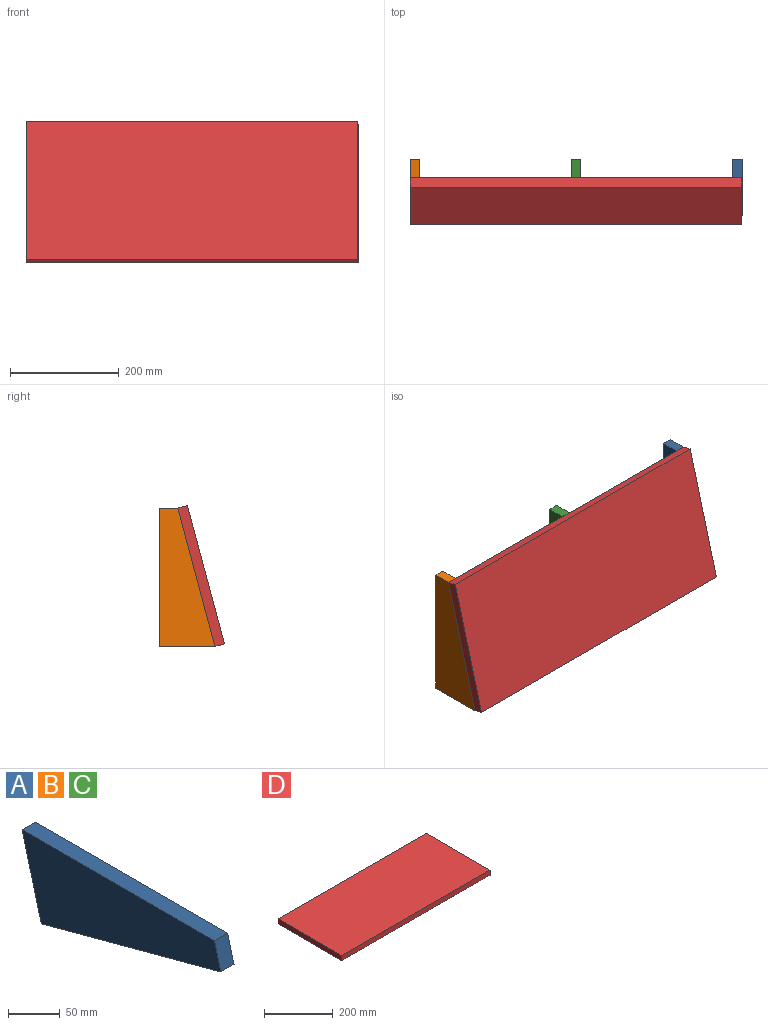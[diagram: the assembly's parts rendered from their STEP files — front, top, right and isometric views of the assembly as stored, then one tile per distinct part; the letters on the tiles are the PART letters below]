
ASSEMBLY  parts=4 mates=3
PART A: 6 faces, bbox 18x271.6x98.1 mm
  f0: plane 262.96x18.03mm, normal (0,0,1), area 4742.2mm2, adj f1,f3,f4,f5
  f1: plane 32.4x18.03mm, normal (0,-0.97,0.26), area 604.9mm2, adj f0,f2,f4,f5
  f2: plane 245.35x65.74mm, normal (0,-0.26,-0.97), area 4580.6mm2, adj f1,f3,f4,f5
  f3: plane 98.14x26.3mm, normal (0,0.97,-0.26), area 1832.3mm2, adj f0,f2,f4,f5
  f4: plane 271.64x98.14mm, normal (-1,0,0), area 17162.9mm2, adj f0,f1,f2,f3
  f5: plane 271.64x98.14mm, normal (1,0,0), area 17162.9mm2, adj f0,f1,f2,f3
PART B: same geometry as A
PART C: same geometry as A
PART D: 6 faces, bbox 609.6x263x18 mm
  f0: plane 609.6x18.03mm, normal (0,-1,0), area 10993.5mm2, adj f1,f3,f4,f5
  f1: plane 262.96x18.03mm, normal (1,0,0), area 4742.2mm2, adj f0,f2,f4,f5
  f2: plane 609.6x18.03mm, normal (0,1,0), area 10993.5mm2, adj f1,f3,f4,f5
  f3: plane 262.96x18.03mm, normal (-1,0,0), area 4742.2mm2, adj f0,f2,f4,f5
  f4: plane 609.6x262.96mm, normal (0,0,1), area 160300.5mm2, adj f0,f1,f2,f3
  f5: plane 609.6x262.96mm, normal (0,0,-1), area 160300.5mm2, adj f0,f1,f2,f3
PLACE A rot(axis=(0,-0.61,0.79),180deg) t=(7227.32,-98.96,157.07)mm
PLACE B rot(axis=(0,-0.61,0.79),180deg) t=(6635.75,-98.96,157.07)mm
PLACE C rot(axis=(0,-0.61,0.79),180deg) t=(6931.53,-98.96,157.07)mm
PLACE D rot(axis=(1,0,0),75deg) t=(-6026.15,-109.79,116.65)mm
MATE fastened D.f5 <-> B.f0  axis (0,0.97,-0.26) through (0,-101.6,0)mm
MATE fastened D.f5 <-> C.f0  axis (0,0.97,-0.26) through (304.8,-101.6,0)mm
MATE fastened D.f5 <-> A.f0  axis (0,0.97,-0.26) through (609.6,-101.6,0)mm
